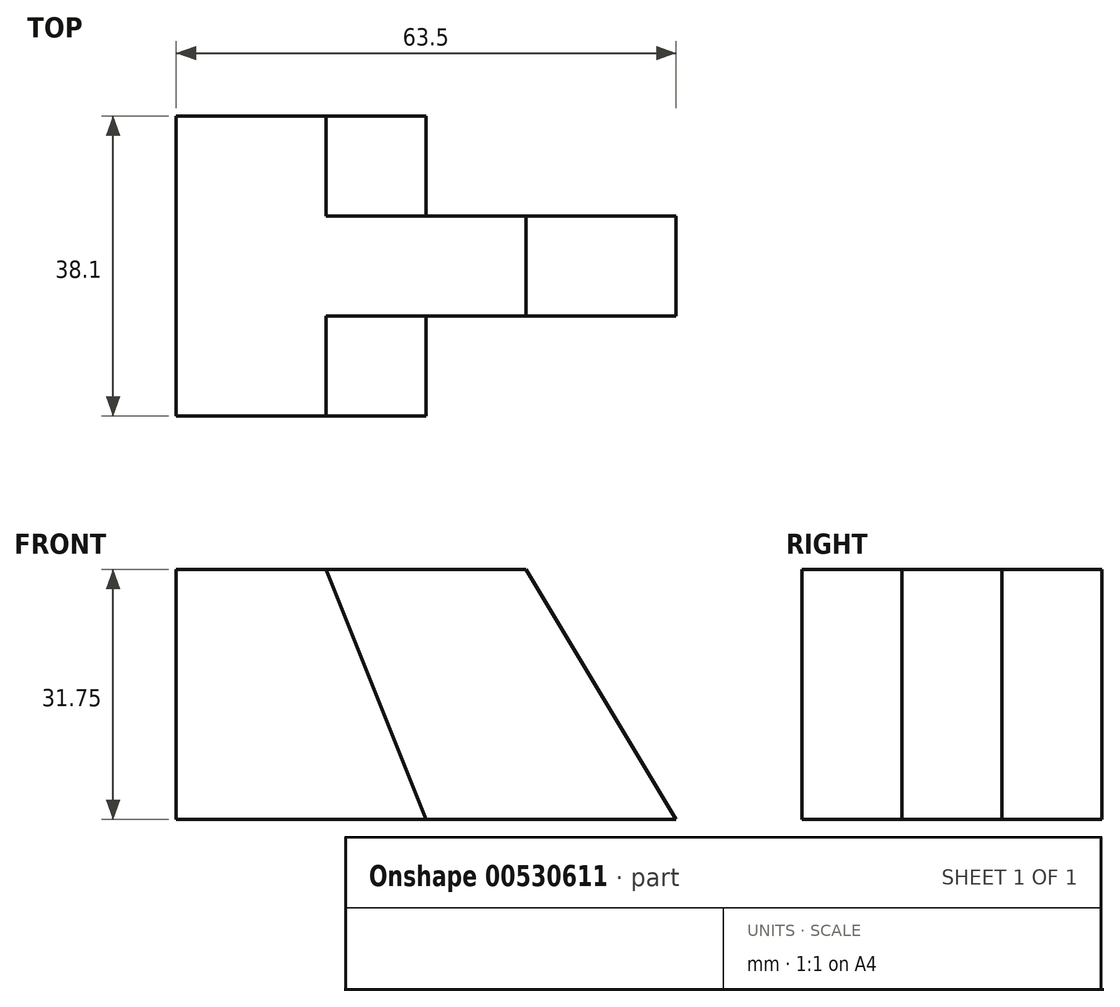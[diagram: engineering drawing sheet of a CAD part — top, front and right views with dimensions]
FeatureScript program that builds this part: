
annotation { "Feature Type Name" : "Feature", "Feature Type Description" : "" }
export const myFeature = defineFeature(function(context is Context, id is Id, definition is map)
    precondition{}
    {
        {
            var Q0;
            Q0=qCreatedBy(makeId("Top.planeOp"),FACE);
            var sketch = newSketch(context, id + "F0", { "sketchPlane" : qUnion([Q0])});
            skLineSegment(sketch, "E0", {"start": v(-53.05, -4.17) * mm, "end": v(-21.3, -4.17) * mm});
            skLineSegment(sketch, "E1", {"start": v(-21.3, -4.17) * mm, "end": v(-21.3, -16.87) * mm});
            skLineSegment(sketch, "E2", {"start": v(-21.3, -16.87) * mm, "end": v(10.45, -16.87) * mm});
            skLineSegment(sketch, "E3", {"start": v(10.45, -16.87) * mm, "end": v(10.45, -29.57) * mm});
            skLineSegment(sketch, "E4", {"start": v(10.45, -29.57) * mm, "end": v(-21.3, -29.57) * mm});
            skLineSegment(sketch, "E5", {"start": v(-21.3, -29.57) * mm, "end": v(-21.3, -42.27) * mm});
            skLineSegment(sketch, "E6", {"start": v(-21.3, -42.27) * mm, "end": v(-53.05, -42.27) * mm});
            skLineSegment(sketch, "E7", {"start": v(-53.05, -42.27) * mm, "end": v(-53.05, -4.17) * mm});
            skSolve(sketch);
        }
        {
            var Q0;
            Q0=makeQuery(id+"F0.imprint","IMPRINT",FACE,{"disambiguationData":[TD([[makeQuery(id+"F0.imprint","IMPRINT",EDGE,{"derivedFrom":sQuery(id+"F0.wireOp",EDGE,"E0")}),-1.0]])]});
            extrude(context, id + "F1", {"entities" : qUnion([Q0]), "depth" : 31.75 * mm, "offsetDistance" : 25.4 * mm});
        }
        {
            var Q0;
            Q0=makeQuery(id+"F1.opExtrude","SWEPT_FACE",FACE,{"disambiguationData":[OSD([sQuery(id+"F0.wireOp",EDGE,"E6")])]});
            var sketch = newSketch(context, id + "F2", { "sketchPlane" : qUnion([Q0])});
            skLineSegment(sketch, "E8", {"start": v(-34, 31.75) * mm, "end": v(-21.3, 0) * mm});
            skSolve(sketch);
        }
        {
            var Q0;
            {var subQ0=sQuery(id+"F2.wireOp",EDGE,"E8");Q0=makeQuery(id+"F2.imprint","IMPRINT",FACE,{"disambiguationData":[TD([[makeQuery(id+"F2.imprint","IMPRINT",EDGE,{"derivedFrom":subQ0}),1.0]])]});}
            extrude(context, id + "F3", {"entities" : qUnion([Q0]), "operationType" : NewBodyOperationType.REMOVE, "oppositeDirection" : true, "depth" : 12.7 * mm, "offsetDistance" : 25.4 * mm});
        }
        {
            var Q0;
            Q0=makeQuery(id+"F3.boolean.opBoolean","MERGE",FACE,{"derivedFrom":[makeQuery(id+"F1.opExtrude","SWEPT_FACE",FACE,{"disambiguationData":[OSD([sQuery(id+"F0.wireOp",EDGE,"E4")])]}),makeQuery(id+"F3.opExtrude","CAP_FACE",FACE,{"disambiguationData":[OSD([sQuery(id+"F0.wireOp",EDGE,"E5"),sQuery(id+"F0.wireOp",EDGE,"E6"),sQuery(id+"F2.wireOp",EDGE,"E8")])],"isStart":false})]});
            var sketch = newSketch(context, id + "F4", { "sketchPlane" : qUnion([Q0])});
            skLineSegment(sketch, "E9", {"start": v(-8.6, 31.75) * mm, "end": v(10.45, 0) * mm});
            skSolve(sketch);
        }
        {
            var Q0;
            {var subQ0=sQuery(id+"F4.wireOp",EDGE,"E9");Q0=makeQuery(id+"F4.imprint","IMPRINT",FACE,{"disambiguationData":[TD([[makeQuery(id+"F4.imprint","IMPRINT",EDGE,{"derivedFrom":subQ0}),1.0]])]});}
            extrude(context, id + "F5", {"entities" : qUnion([Q0]), "operationType" : NewBodyOperationType.REMOVE, "endBound" : BoundingType.THROUGH_ALL, "oppositeDirection" : true, "depth" : 12.7 * mm, "offsetDistance" : 25.4 * mm});
        }
        {
            var Q0;
            Q0=makeQuery(id+"F1.opExtrude","SWEPT_FACE",FACE,{"disambiguationData":[OSD([sQuery(id+"F0.wireOp",EDGE,"E0")])]});
            var sketch = newSketch(context, id + "F6", { "sketchPlane" : qUnion([Q0])});
            skLineSegment(sketch, "E10", {"start": v(34, 31.75) * mm, "end": v(21.3, 0) * mm});
            skSolve(sketch);
        }
        {
            var Q0;
            {var subQ0=sQuery(id+"F6.wireOp",EDGE,"E10");Q0=makeQuery(id+"F6.imprint","IMPRINT",FACE,{"disambiguationData":[TD([[makeQuery(id+"F6.imprint","IMPRINT",EDGE,{"derivedFrom":subQ0}),-1.0]])]});}
            extrude(context, id + "F7", {"entities" : qUnion([Q0]), "operationType" : NewBodyOperationType.REMOVE, "oppositeDirection" : true, "depth" : 12.7 * mm, "offsetDistance" : 25.4 * mm});
        }
    });
